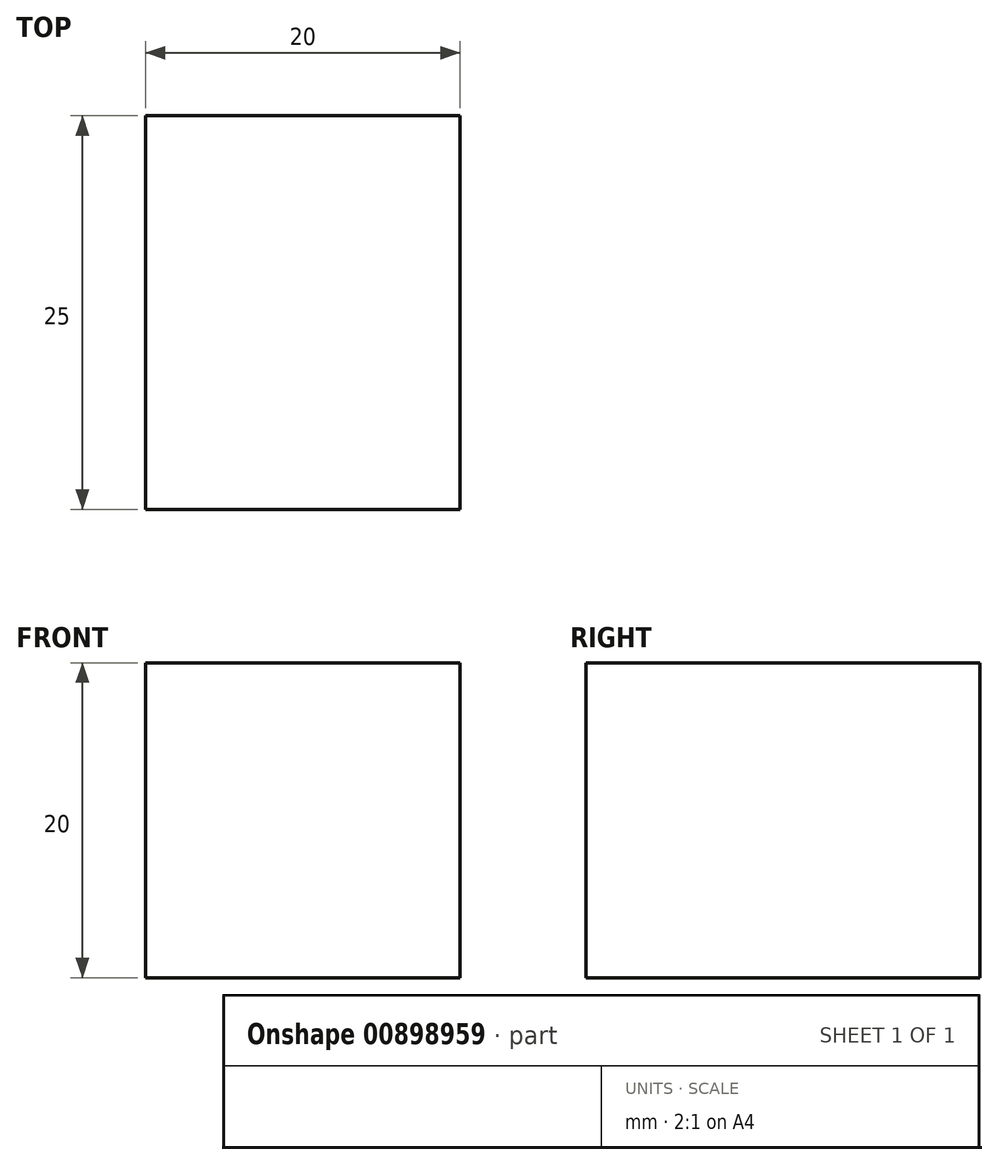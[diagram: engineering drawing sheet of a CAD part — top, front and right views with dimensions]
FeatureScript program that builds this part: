
annotation { "Feature Type Name" : "Feature", "Feature Type Description" : "" }
export const myFeature = defineFeature(function(context is Context, id is Id, definition is map)
    precondition{}
    {
        {
            var Q0;
            Q0=qCreatedBy(makeId("Front.planeOp"),FACE);
            var sketch = newSketch(context, id + "F0", { "sketchPlane" : qUnion([Q0])});
            skLineSegment(sketch, "E0.bottom", {"start": v(-10, 30) * mm, "end": v(10, 30) * mm});
            skLineSegment(sketch, "E0.top", {"start": v(-10, 10) * mm, "end": v(10, 10) * mm});
            skLineSegment(sketch, "E0.left", {"start": v(-10, 30) * mm, "end": v(-10, 10) * mm});
            skLineSegment(sketch, "E0.right", {"start": v(10, 30) * mm, "end": v(10, 10) * mm});
            skSolve(sketch);
        }
        {
            var Q0;
            Q0=makeQuery(id+"F0.imprint","IMPRINT",FACE,{"disambiguationData":[TD([[makeQuery(id+"F0.imprint","IMPRINT",EDGE,{"derivedFrom":sQuery(id+"F0.wireOp",EDGE,"E0.bottom")}),-1.0]])]});
            extrude(context, id + "F1", {"entities" : qUnion([Q0]), "depth" : 25 * mm, "offsetDistance" : 25 * mm});
        }
    });
